# Revit family: Domotics-DomesticRanges-GEWISS-SYSTEM_POWER-SOCKET-OUTLET_DEU
name_source: partatom
category: Apparecchi elettrici
revit_build: Autodesk Revit 2016 (Build: 20161004_0715(x64)
units: mm (PartAtom-declared; Revit-internal decimal feet)

## family parameters
Condiviso = Sì
Host = Superficie
Mantenere orientamento annotazione = Sì
Punto di calcolo locali = Sì
Quota connettore circolare = Usa diametro
Taglio con vuoti quando caricato = No
Tipo di parte = Normale

## types (5) — shared parameters
Carico apparente = 0 VA
Catalogue = DOMOTICS
Catalogue Range = SYSTEM - DOMESTIC RANGE
Description. = Socket-outlet 16 A
Description: = 2P+E - 16A
Electrocod = 0131
For plug pins = Ã˜ 4.8 mm
IDF = dc766728-6194-4f2d-9aeb-2b383f6f0fa6
IDT = 69867918-0b99-4f07-922d-dcc2e49a9ce3
Immagine tipo = GW21265.jpg
N. poli = 1
No. SYSTEM modules = 2
Produttore = GEWISS S.p.A.
Prospetto di default = 1219 mm
SEO = Socket outlet
Standard = German
Standard: = German
TIPO_ = System Prese Ger_GENERICO : GW21265 Presa 2P+T 16A standard Tedesco nero
TXT ELETTRICO = 16
Technical sheet = https://www.gewiss.com
URL = https://www.gewiss.com
Version file RFA = 19.4
Volt = 230 V
Voltage = 250 V ac
Voltage: = 250 V ac

## per-type parameters (varying)
| type | Colour | Descrizione | EAN code | Modello | Type | Type: |
| GW20265 - 2P+E 16A german std s.-outlet white | White | 2P+E 16A GERMAN STD S.-OUTLET SY/WT | 8011564038516 | GW20265 |  |  |
| GW21265 - 2P+E 16A german std s.-outlet black | Black | 2P+E 16A GERMAN STD S.-OUTLET SY/BK | 8011564128477 | GW21265 |  |  |
| GW20297 - 2P+E 16A germ.st.red socket | Red | 2P+E 16A GERM.ST.RED SOCKET | 8011564044883 | GW20297 | For allocated lines | For allocated lines |
| GW20283 - 2P+E 16A germ.st.green socket | Green | 2P+E 16A GERM.ST.GREEN SOCKET | 8011564079441 | GW20283 | For allocated lines | For allocated lines |
| GW20288 - 2P+E 16A germ.st.orange socket | Orange | 2P+E 16A GERM.ST.ORANGE SOCKET | 8011564079472 | GW20288 | For allocated lines | For allocated lines |

## geometry (parser evidence)
native form markers: Sweep x2
no freeform markers — native parametric forms only
